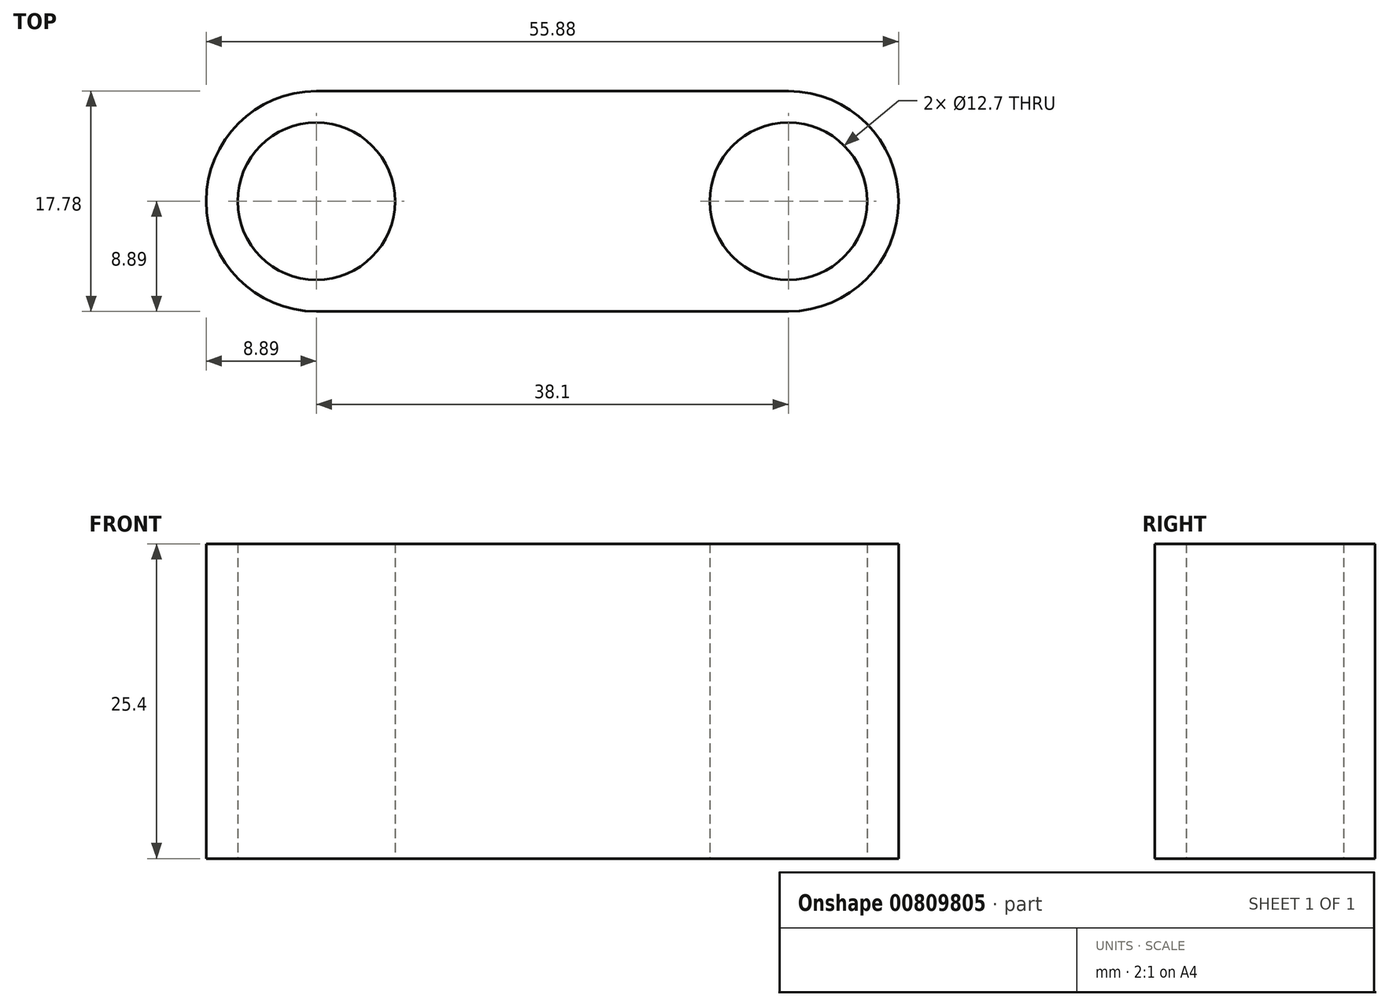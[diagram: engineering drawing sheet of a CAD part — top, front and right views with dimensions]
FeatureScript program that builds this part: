
annotation { "Feature Type Name" : "Feature", "Feature Type Description" : "" }
export const myFeature = defineFeature(function(context is Context, id is Id, definition is map)
    precondition{}
    {
        {
            var Q0;
            Q0=qCreatedBy(makeId("Top.planeOp"),FACE);
            var sketch = newSketch(context, id + "F0", { "sketchPlane" : qUnion([Q0])});
            skCircle(sketch, "E0", {"center": v(0, 0) * mm, "radius": 6.35 * mm});
            skCircle(sketch, "E1", {"center": v(38.1, 0) * mm, "radius": 6.35 * mm});
            skCircle(sketch, "E2", {"center": v(0, 0) * mm, "radius": 8.9 * mm});
            skCircle(sketch, "E3", {"center": v(38.1, 0) * mm, "radius": 8.9 * mm});
            skLineSegment(sketch, "E4", {"start": v(0, 8.9) * mm, "end": v(38.1, 8.89) * mm});
            skLineSegment(sketch, "E5", {"start": v(0, -8.9) * mm, "end": v(38.1, -8.89) * mm});
            skSolve(sketch);
        }
        {
            var Q0;
            Q0=qSketchRegion(id+"F0",true);
            extrude(context, id + "F1", {"entities" : qUnion([Q0]), "depth" : 25.4 * mm, "offsetDistance" : 25.4 * mm});
        }
    });
